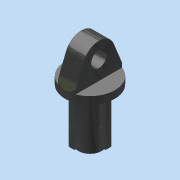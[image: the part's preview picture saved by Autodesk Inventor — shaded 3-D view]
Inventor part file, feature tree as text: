
AUTODESK INVENTOR PART (.ipt)
format: ipt  version: 2011 SP1 (Build 150282100, 282)  size: 154,112 bytes
history: native  units: in
note: dims shown in document units (in); Inventor stores cm internally (conversion verified against a paired STEP export)
features: extrude x5, sketch x5
ambient origin geometry x8: Origin, YZ Plane, XZ Plane, XY Plane, X Axis, Y Axis, Z Axis, Center Point
feature tree (10):
  extrude  "Extrusion7"  Depth=0.1in TaperAngle=0.0deg
  extrude  "Extrusion8"  Depth=0.21in
  extrude  "Extrusion9"  Depth=0.24in TaperAngle=0.0deg
  extrude  "Extrusion10"  Depth=0.156in
  extrude  "Extrusion11"  Depth=0.5in
  sketch  "Sketch8"  dims[d28=0.67in d29=0.1in d30=0.0in]
  sketch  "Sketch9"  dims[d31=0.43in d32=0.21in]
  sketch  "Sketch10"  dims[d33=0.47in d34=0.24in d35=0.0in]
  sketch  "Sketch11"  dims[d36=0.5in d37=0.0in d38=0.156in]
  sketch  "Sketch12"  dims[d39=0.35in d40=0.5in d41=0.08in d42=0.04in d43=1.5748in d45=360.0deg d47=0.62in d48=0.0in d49=0.31in d50=0.08in d51=0.0in]
